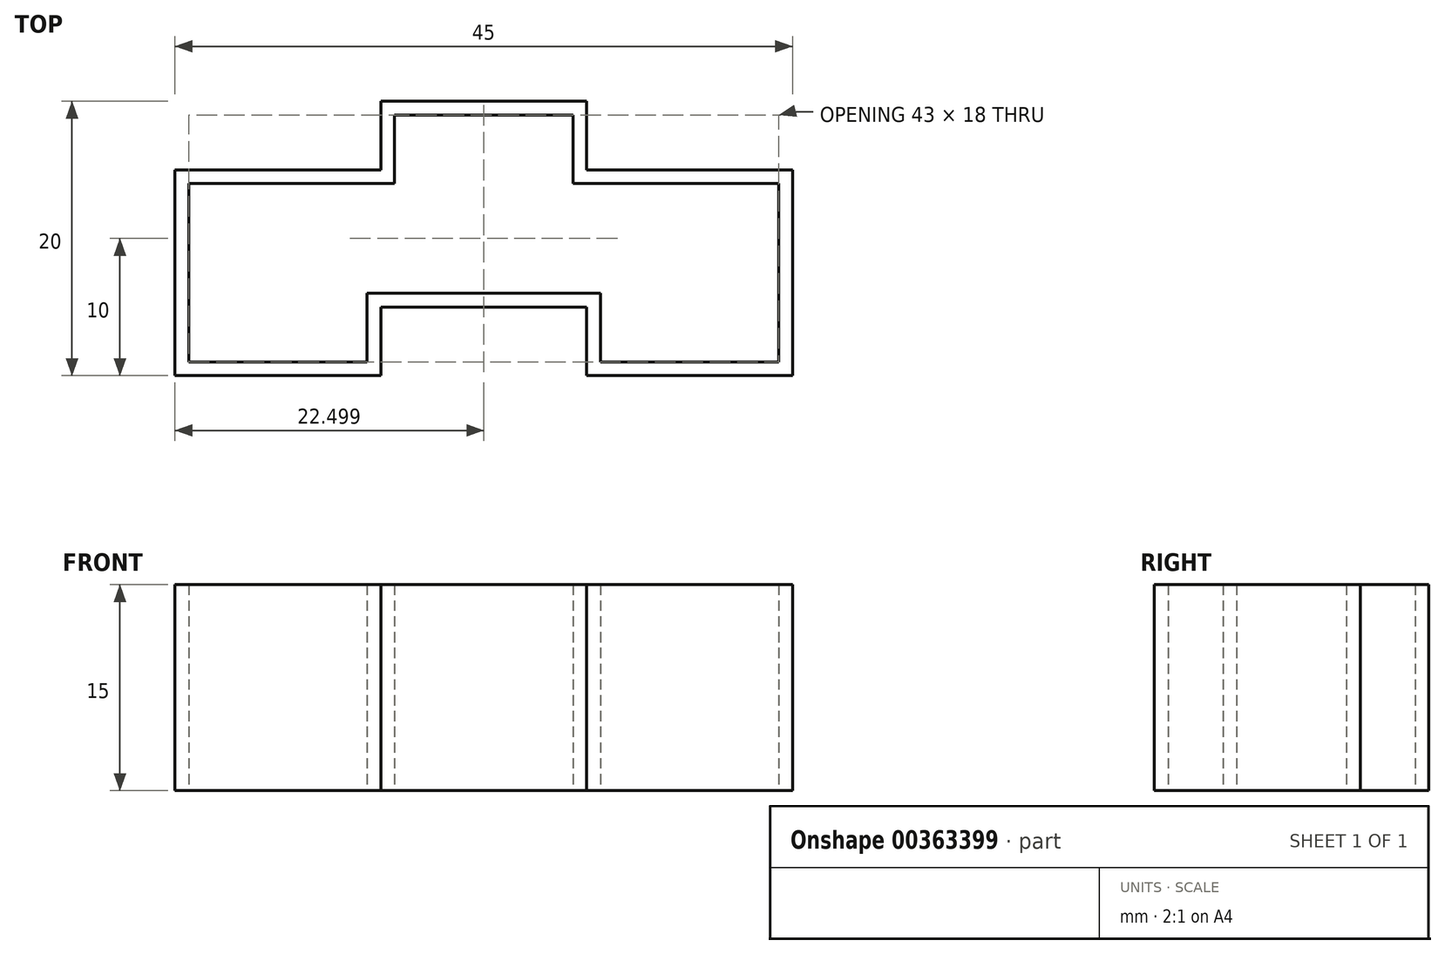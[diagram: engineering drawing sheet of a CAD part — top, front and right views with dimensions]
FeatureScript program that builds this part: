
annotation { "Feature Type Name" : "Feature", "Feature Type Description" : "" }
export const myFeature = defineFeature(function(context is Context, id is Id, definition is map)
    precondition{}
    {
        {
            assignVariable(context, id + "F0", {"name" : "Size", "anyValue" : 15});
        }
        {
            var Q0;
            Q0=qCreatedBy(makeId("Top.planeOp"),FACE);
            var sketch = newSketch(context, id + "F1", { "sketchPlane" : qUnion([Q0])});
            skLineSegment(sketch, "E0.bottom", {"start": v(-24.33, 0) * mm, "end": v(-39.33, 0) * mm});
            skLineSegment(sketch, "E0.top", {"start": v(-24.33, 15) * mm, "end": v(-39.33, 15) * mm});
            skLineSegment(sketch, "E0.left", {"start": v(-24.33, 0) * mm, "end": v(-24.33, 15) * mm});
            skLineSegment(sketch, "E0.right", {"start": v(-39.33, 0) * mm, "end": v(-39.33, 15) * mm});
            skLineSegment(sketch, "E1.bottom", {"start": v(-9.33, 0) * mm, "end": v(5.67, 0) * mm});
            skLineSegment(sketch, "E1.top", {"start": v(-9.33, 15) * mm, "end": v(5.67, 15) * mm});
            skLineSegment(sketch, "E1.left", {"start": v(-9.33, 0) * mm, "end": v(-9.33, 15) * mm});
            skLineSegment(sketch, "E1.right", {"start": v(5.67, 0) * mm, "end": v(5.67, 15) * mm});
            skLineSegment(sketch, "E2.0", {"start": v(-38.33, 1) * mm, "end": v(-38.33, 14) * mm});
            skLineSegment(sketch, "E2.1", {"start": v(-25.33, 1) * mm, "end": v(-38.33, 1) * mm});
            skLineSegment(sketch, "E2.2", {"start": v(-25.33, 1) * mm, "end": v(-25.33, 14) * mm});
            skLineSegment(sketch, "E2.3", {"start": v(-25.33, 14) * mm, "end": v(-38.33, 14) * mm});
            skLineSegment(sketch, "E3.0", {"start": v(-8.33, 1) * mm, "end": v(-8.33, 14) * mm});
            skLineSegment(sketch, "E3.1", {"start": v(-8.33, 1) * mm, "end": v(4.67, 1) * mm});
            skLineSegment(sketch, "E3.2", {"start": v(4.67, 1) * mm, "end": v(4.67, 14) * mm});
            skLineSegment(sketch, "E3.3", {"start": v(-8.33, 14) * mm, "end": v(4.67, 14) * mm});
            skPoint(sketch, "E4.oppositeSnap0", {"position": v(-9.33, 7.5) * mm});
            skLineSegment(sketch, "E4.bottom", {"start": v(-24.33, 5) * mm, "end": v(-9.33, 5) * mm});
            skLineSegment(sketch, "E4.top", {"start": v(-24.33, 20) * mm, "end": v(-9.33, 20) * mm});
            skLineSegment(sketch, "E4.left", {"start": v(-24.33, 5) * mm, "end": v(-24.33, 20) * mm});
            skLineSegment(sketch, "E4.right", {"start": v(-9.33, 5) * mm, "end": v(-9.33, 20) * mm});
            skLineSegment(sketch, "E5.0", {"start": v(-23.33, 6) * mm, "end": v(-23.33, 19) * mm});
            skLineSegment(sketch, "E5.1", {"start": v(-23.33, 6) * mm, "end": v(-10.33, 6) * mm});
            skLineSegment(sketch, "E5.2", {"start": v(-10.33, 6) * mm, "end": v(-10.33, 19) * mm});
            skLineSegment(sketch, "E5.3", {"start": v(-23.33, 19) * mm, "end": v(-10.33, 19) * mm});
            skLineSegment(sketch, "E6", {"start": v(-25.33, 6) * mm, "end": v(-8.33, 6) * mm});
            skLineSegment(sketch, "E7", {"start": v(-25.33, 14) * mm, "end": v(-8.33, 14) * mm});
            skSolve(sketch);
        }
        {
            var Q0;
            Q0=makeQuery(id+"F1.imprint","IMPRINT",FACE,{"disambiguationData":[TD([[makeQuery(id+"F1.imprint","IMPRINT",EDGE,{"derivedFrom":sQuery(id+"F1.wireOp",EDGE,"E0.bottom")}),-1.0]])]});
            var Q1;
            {var subQ5=sQuery(id+"F1.wireOp",EDGE,"E4.bottom");Q1=makeQuery(id+"F1.imprint","IMPRINT",FACE,{"disambiguationData":[TD([[makeQuery(id+"F1.imprint","IMPRINT",EDGE,{"derivedFrom":subQ5}),1.0]])]});}
            var Q2;
            Q2=makeQuery(id+"F1.imprint","IMPRINT",FACE,{"disambiguationData":[TD([[makeQuery(id+"F1.imprint","IMPRINT",EDGE,{"derivedFrom":sQuery(id+"F1.wireOp",EDGE,"E1.bottom")}),1.0]])]});
            var Q3;
            {var subQ6=sQuery(id+"F1.wireOp",EDGE,"E4.top");Q3=makeQuery(id+"F1.imprint","IMPRINT",FACE,{"disambiguationData":[TD([[makeQuery(id+"F1.imprint","IMPRINT",EDGE,{"derivedFrom":subQ6}),-1.0]])]});}
            extrude(context, id + "F2", {"entities" : qUnion([Q0, Q1, Q2, Q3]), "depth" : (getVariable(context, 'Size')) * mm});
        }
    });
